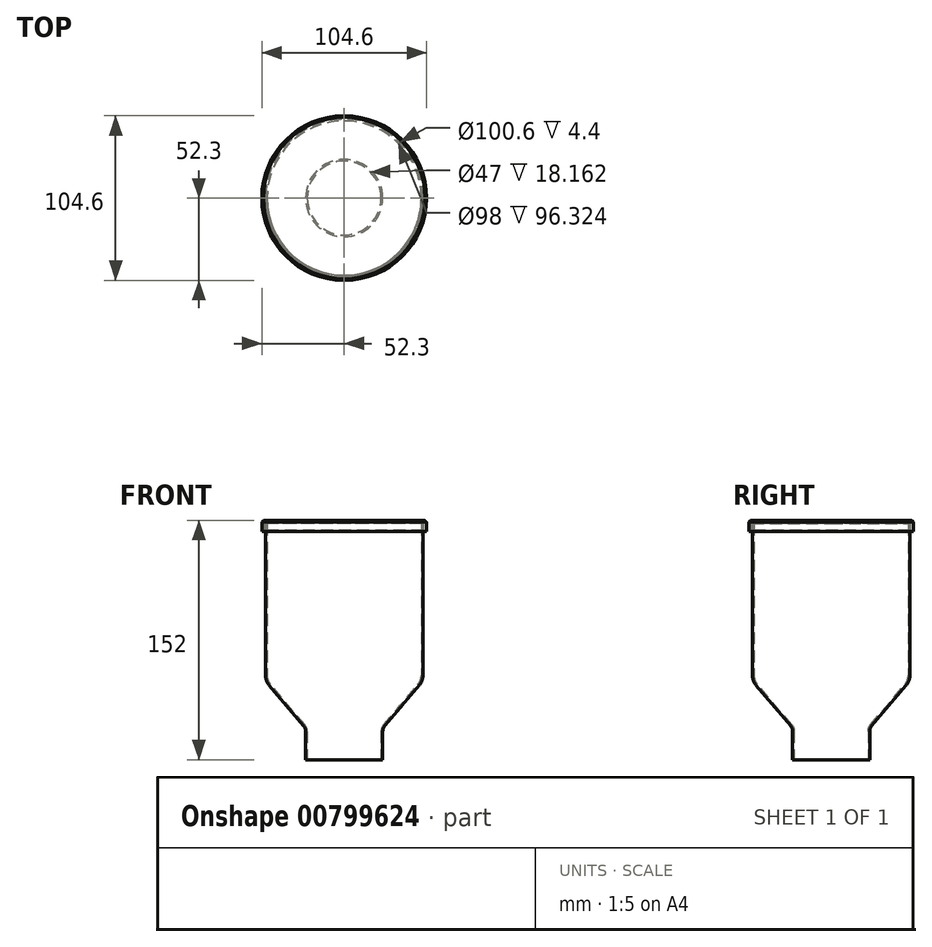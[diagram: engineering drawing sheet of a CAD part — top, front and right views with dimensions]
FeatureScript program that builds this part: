
annotation { "Feature Type Name" : "Feature", "Feature Type Description" : "" }
export const myFeature = defineFeature(function(context is Context, id is Id, definition is map)
    precondition{}
    {
        {
            var Q0;
            Q0=qCreatedBy(makeId("Top.planeOp"),FACE);
            var sketch = newSketch(context, id + "F0", { "sketchPlane" : qUnion([Q0])});
            skCircle(sketch, "E0", {"center": v(0, 0) * mm, "radius": 24.5 * mm});
            skSolve(sketch);
        }
        {
            var Q0;
            Q0 = qSketchRegion(id + "F0", true);
            extrude(context, id + "F1", {"entities" : qUnion([Q0]), "depth" : 20 * mm, "offsetDistance" : 25 * mm});
        }
        {
            var Q0;
            Q0=makeQuery(id+"F1.opExtrude","CAP_FACE",FACE,{"disambiguationData":[OSD([sQuery(id+"F0.wireOp",EDGE,"E0")])],"isStart":false});
            cPlane(context, id + "F2", {"entities" : qUnion([Q0]), "cplaneType" : CPlaneType.OFFSET, "offset" : 30 * mm, "width" : 150 * mm, "height" : 150 * mm});
        }
        {
            var Q0;
            Q0=qCreatedBy(id+"F2.planeOp",FACE);
            var sketch = newSketch(context, id + "F3", { "sketchPlane" : qUnion([Q0])});
            skCircle(sketch, "E1", {"center": v(0, 0) * mm, "radius": 50 * mm});
            skSolve(sketch);
        }
        {
            var Q1;
            Q1=makeQuery(id+"F1.opExtrude","CAP_FACE",FACE,{"disambiguationData":[OSD([sQuery(id+"F0.wireOp",EDGE,"E0")])],"isStart":false});
            var Q2;
            Q2=makeQuery(id+"F3.imprint","IMPRINT",FACE,{"disambiguationData":[TD([[makeQuery(id+"F3.imprint","IMPRINT",EDGE,{"derivedFrom":sQuery(id+"F3.wireOp",EDGE,"E1")}),1.0]])]});
            loft(context, id + "F4", {"operationType" : NewBodyOperationType.ADD, "sheetProfilesArray" : [{ "sheetProfileEntities" : qUnion([Q1]) }, { "sheetProfileEntities" : qUnion([Q2]) }]});
        }
        {
            var Q0;
            Q0=makeQuery(id+"F4.opLoft","CAP_FACE",FACE,{"disambiguationData":[OSD([makeQuery(id+"F3.imprint","IMPRINT",FACE,{"disambiguationData":[TD([[makeQuery(id+"F3.imprint","IMPRINT",EDGE,{"derivedFrom":sQuery(id+"F3.wireOp",EDGE,"E1")}),1.0]])]})])],"isStart":true});
            extrude(context, id + "F5", {"entities" : qUnion([Q0]), "operationType" : NewBodyOperationType.ADD, "depth" : 100 * mm, "offsetDistance" : 25 * mm});
        }
        {
            var Q0;
            {var subQ0=sQuery(id+"F0.wireOp",EDGE,"E0");Q0=makeQuery(id+"F4.boolean.opBoolean","MERGE",EDGE,{"derivedFrom":[makeQuery(id+"F1.opExtrude","CAP_EDGE",EDGE,{"disambiguationData":[OSD([subQ0])],"isStart":false}),makeQuery(id+"F4.opLoft","MID_CAP_EDGE",EDGE,{"disambiguationData":[OSD([subQ0])],"capPos":0.0})]});}
            fillet(context, id + "F6", {"entities" : qUnion([Q0]), "radius" : 5 * mm, "tangentPropagation" : true, "allowEdgeOverflow" : false});
        }
        {
            var Q0;
            {var subQ0=sQuery(id+"F3.wireOp",EDGE,"E1");Q0=makeQuery(id+"F5.boolean.opBoolean","MERGE",EDGE,{"derivedFrom":[makeQuery(id+"F4.opLoft","MID_CAP_EDGE",EDGE,{"disambiguationData":[OSD([subQ0])],"capPos":1.0}),makeQuery(id+"F5.opExtrude","CAP_EDGE",EDGE,{"disambiguationData":[OSD([subQ0])],"isStart":true})]});}
            fillet(context, id + "F7", {"entities" : qUnion([Q0]), "radius" : 10 * mm, "tangentPropagation" : true, "allowEdgeOverflow" : false});
        }
        {
            var Q0;
            Q0=makeQuery(id+"F1.opExtrude","CAP_FACE",FACE,{"disambiguationData":[OSD([sQuery(id+"F0.wireOp",EDGE,"E0")])],"isStart":true});
            var Q1;
            Q1=makeQuery(id+"F5.opExtrude","CAP_FACE",FACE,{"disambiguationData":[OSD([makeQuery(id+"F3.imprint","IMPRINT",FACE,{"disambiguationData":[TD([[makeQuery(id+"F3.imprint","IMPRINT",EDGE,{"derivedFrom":sQuery(id+"F3.wireOp",EDGE,"E1")}),1.0]])]})])],"isStart":false});
            shell(context, id + "F8", {"entities" : qUnion([Q0, Q1]), "thickness" : 1 * mm});
        }
        {
            var Q0;
            Q0=makeQuery(id+"F5.opExtrude","CAP_FACE",FACE,{"disambiguationData":[OSD([makeQuery(id+"F3.imprint","IMPRINT",FACE,{"disambiguationData":[TD([[makeQuery(id+"F3.imprint","IMPRINT",EDGE,{"derivedFrom":sQuery(id+"F3.wireOp",EDGE,"E1")}),1.0]])]})])],"isStart":false});
            var sketch = newSketch(context, id + "F9", { "sketchPlane" : qUnion([Q0])});
            skCircle(sketch, "E2.0", {"center": v(0, 0) * mm, "radius": 50.3 * mm});
            skCircle(sketch, "E3.0", {"center": v(0, 0) * mm, "radius": 52.3 * mm});
            skSolve(sketch);
        }
        {
            var Q0;
            {var subQ0=sQuery(id+"F3.wireOp",EDGE,"E1");Q0=makeQuery(id+"F9.imprint","IMPRINT",FACE,{"disambiguationData":[TD([[makeQuery(id+"F9.imprint","IMPRINT",EDGE,{"derivedFrom":makeQuery(id+"F8.opShell","OFFSET_EDGE",EDGE,{"disambiguationData":[OSD([subQ0]),TDD([makeQuery(id+"F5.opExtrude","CAP_EDGE",EDGE,{"disambiguationData":[OSD([subQ0])],"isStart":false})])]})}),1.0]])]});}
            var Q1;
            {var subQ0=sQuery(id+"F3.wireOp",EDGE,"E1");var subQ1=makeQuery(id+"F5.opExtrude","CAP_EDGE",EDGE,{"disambiguationData":[OSD([subQ0])],"isStart":false});Q1=makeQuery(id+"F9.imprint","IMPRINT",FACE,{"disambiguationData":[TD([[makeQuery(id+"F9.imprint","IMPRINT",EDGE,{"derivedFrom":subQ1}),1.0]])]});}
            var Q2;
            Q2=makeQuery(id+"F9.imprint","IMPRINT",FACE,{"disambiguationData":[TD([[makeQuery(id+"F9.imprint","IMPRINT",EDGE,{"derivedFrom":sQuery(id+"F9.wireOp",EDGE,"E2.0")}),1.0]])]});
            var Q3;
            Q3=makeQuery(id+"F9.imprint","IMPRINT",FACE,{"disambiguationData":[TD([[makeQuery(id+"F9.imprint","IMPRINT",EDGE,{"derivedFrom":sQuery(id+"F9.wireOp",EDGE,"E2.0")}),-1.0]])]});
            extrude(context, id + "F10", {"entities" : qUnion([Q0, Q1, Q2, Q3]), "depth" : 2 * mm, "offsetDistance" : 25 * mm});
        }
        {
            var Q0;
            Q0=makeQuery(id+"F9.imprint","IMPRINT",FACE,{"disambiguationData":[TD([[makeQuery(id+"F9.imprint","IMPRINT",EDGE,{"derivedFrom":sQuery(id+"F9.wireOp",EDGE,"E2.0")}),-1.0]])]});
            extrude(context, id + "F11", {"entities" : qUnion([Q0]), "operationType" : NewBodyOperationType.ADD, "oppositeDirection" : true, "depth" : 5 * mm, "offsetDistance" : 25 * mm});
        }
        {
            var Q0;
            Q0=makeQuery(id+"F10.opExtrude","CAP_FACE",FACE,{"disambiguationData":[OSD([sQuery(id+"F9.wireOp",EDGE,"E3.0")])],"isStart":false});
            chamfer(context, id + "F12", {"entities" : qUnion([Q0]), "width" : 1 * mm, "tangentPropagation" : true});
        }
        {
            var Q0;
            Q0=makeQuery(id+"F11.opExtrude","CAP_EDGE",EDGE,{"disambiguationData":[OSD([sQuery(id+"F9.wireOp",EDGE,"E2.0")])],"isStart":false});
            chamfer(context, id + "F13", {"entities" : qUnion([Q0]), "width" : 0.6 * mm, "tangentPropagation" : true});
        }
    });
